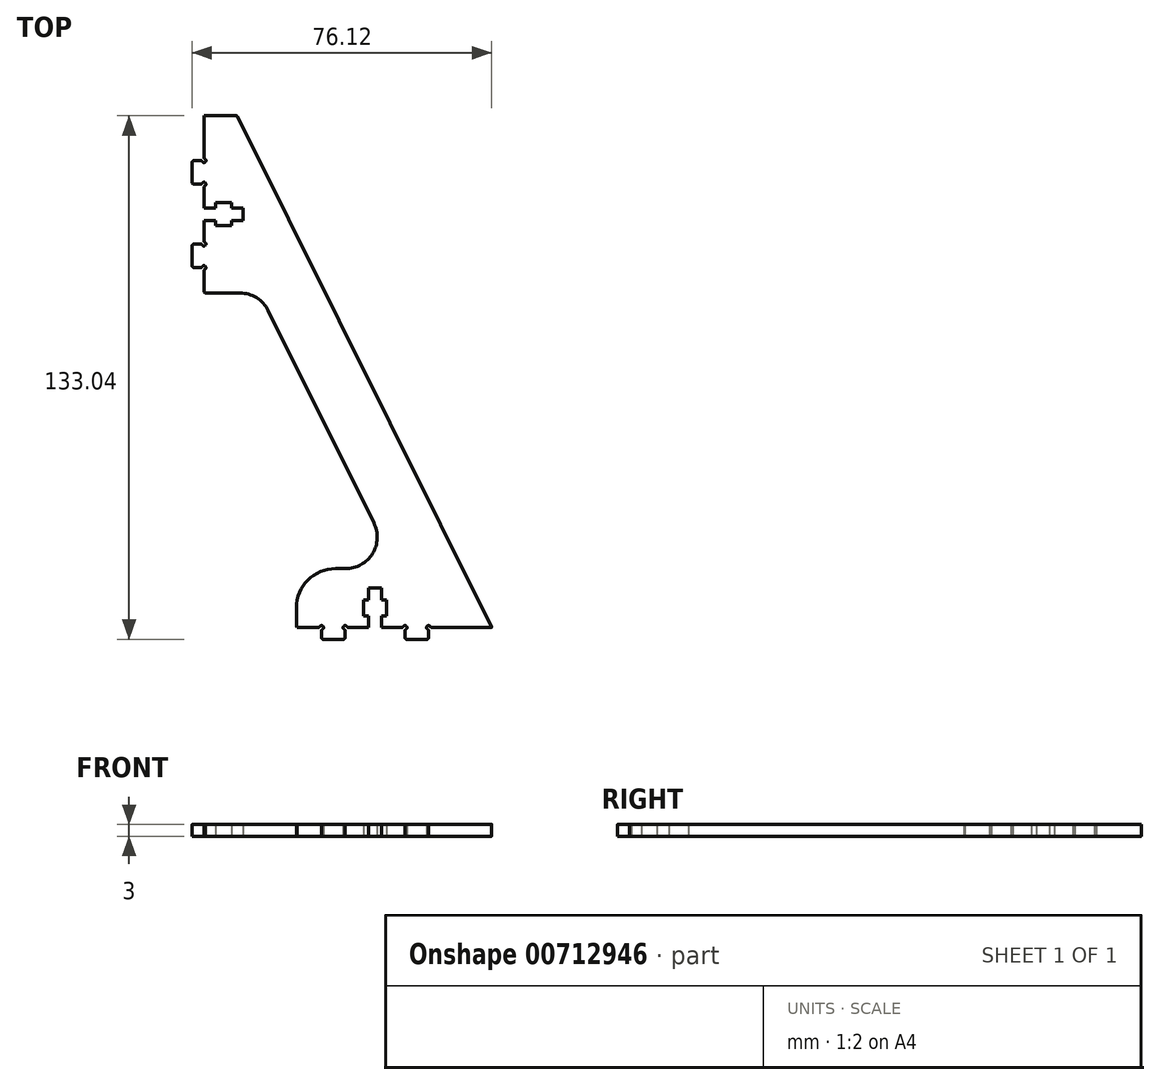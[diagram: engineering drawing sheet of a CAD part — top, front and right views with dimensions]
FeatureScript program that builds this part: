
annotation { "Feature Type Name" : "Feature", "Feature Type Description" : "" }
export const myFeature = defineFeature(function(context is Context, id is Id, definition is map)
    precondition{}
    {
        {
            var Q0;
            Q0=qCreatedBy(makeId("Top.planeOp"),FACE);
            var sketch = newSketch(context, id + "F0", { "sketchPlane" : qUnion([Q0])});
            skArc(sketch, "E0", {"start": v(-6.05, -63.52) * mm, "mid": v(-5.8, -63.45) * mm, "end": v(-5.61, -63.27) * mm});
            skArc(sketch, "E1", {"start": v(-4.93, -63.95) * mm, "mid": v(-4.83, -63.17) * mm, "end": v(-5.61, -63.27) * mm});
            skArc(sketch, "E2", {"start": v(-4.93, -63.95) * mm, "mid": v(-5.11, -64.14) * mm, "end": v(-5.18, -64.39) * mm});
            skLineSegment(sketch, "E3", {"start": v(-5.18, -64.39) * mm, "end": v(-5.18, -66.02) * mm});
            skArc(sketch, "E4", {"start": v(-5.18, -66.02) * mm, "mid": v(-5.04, -66.38) * mm, "end": v(-4.68, -66.52) * mm});
            skLineSegment(sketch, "E5", {"start": v(-4.68, -66.52) * mm, "end": v(0.32, -66.52) * mm});
            skArc(sketch, "E6", {"start": v(0.32, -66.52) * mm, "mid": v(0.67, -66.38) * mm, "end": v(0.82, -66.02) * mm});
            skLineSegment(sketch, "E7", {"start": v(0.82, -66.02) * mm, "end": v(0.82, -64.39) * mm});
            skArc(sketch, "E8", {"start": v(0.82, -64.39) * mm, "mid": v(0.75, -64.14) * mm, "end": v(0.57, -63.95) * mm});
            skArc(sketch, "E9", {"start": v(1.25, -63.27) * mm, "mid": v(0.46, -63.17) * mm, "end": v(0.57, -63.95) * mm});
            skArc(sketch, "E10", {"start": v(1.25, -63.27) * mm, "mid": v(1.43, -63.45) * mm, "end": v(1.68, -63.52) * mm});
            skLineSegment(sketch, "E11", {"start": v(1.68, -63.52) * mm, "end": v(6.82, -63.52) * mm});
            skLineSegment(sketch, "E12", {"start": v(6.82, -63.52) * mm, "end": v(6.82, -60.52) * mm});
            skLineSegment(sketch, "E13", {"start": v(6.82, -60.52) * mm, "end": v(5.54, -60.52) * mm});
            skLineSegment(sketch, "E14", {"start": v(5.54, -60.52) * mm, "end": v(5.54, -56.52) * mm});
            skLineSegment(sketch, "E15", {"start": v(5.54, -56.52) * mm, "end": v(6.82, -56.52) * mm});
            skLineSegment(sketch, "E16", {"start": v(6.82, -56.52) * mm, "end": v(6.82, -53.52) * mm});
            skLineSegment(sketch, "E17", {"start": v(6.82, -53.52) * mm, "end": v(10.02, -53.52) * mm});
            skLineSegment(sketch, "E18", {"start": v(10.02, -53.52) * mm, "end": v(10.02, -56.52) * mm});
            skLineSegment(sketch, "E19", {"start": v(10.02, -56.52) * mm, "end": v(11.3, -56.52) * mm});
            skLineSegment(sketch, "E20", {"start": v(11.3, -56.52) * mm, "end": v(11.3, -60.52) * mm});
            skLineSegment(sketch, "E21", {"start": v(11.3, -60.52) * mm, "end": v(10.02, -60.52) * mm});
            skLineSegment(sketch, "E22", {"start": v(10.02, -60.52) * mm, "end": v(10.02, -63.52) * mm});
            skLineSegment(sketch, "E23", {"start": v(10.02, -63.52) * mm, "end": v(15.15, -63.52) * mm});
            skArc(sketch, "E24", {"start": v(15.15, -63.52) * mm, "mid": v(15.4, -63.45) * mm, "end": v(15.59, -63.27) * mm});
            skArc(sketch, "E25", {"start": v(16.27, -63.95) * mm, "mid": v(16.37, -63.17) * mm, "end": v(15.59, -63.27) * mm});
            skArc(sketch, "E26", {"start": v(16.27, -63.95) * mm, "mid": v(16.09, -64.14) * mm, "end": v(16.02, -64.39) * mm});
            skLineSegment(sketch, "E27", {"start": v(16.02, -64.39) * mm, "end": v(16.02, -66.02) * mm});
            skArc(sketch, "E28", {"start": v(16.02, -66.02) * mm, "mid": v(16.16, -66.38) * mm, "end": v(16.52, -66.52) * mm});
            skLineSegment(sketch, "E29", {"start": v(16.52, -66.52) * mm, "end": v(21.52, -66.52) * mm});
            skArc(sketch, "E30", {"start": v(21.52, -66.52) * mm, "mid": v(21.87, -66.38) * mm, "end": v(22.02, -66.02) * mm});
            skLineSegment(sketch, "E31", {"start": v(22.02, -66.02) * mm, "end": v(22.02, -64.39) * mm});
            skArc(sketch, "E32", {"start": v(22.02, -64.39) * mm, "mid": v(21.95, -64.14) * mm, "end": v(21.77, -63.95) * mm});
            skArc(sketch, "E33", {"start": v(22.45, -63.27) * mm, "mid": v(21.66, -63.17) * mm, "end": v(21.77, -63.95) * mm});
            skArc(sketch, "E34", {"start": v(22.45, -63.27) * mm, "mid": v(22.63, -63.45) * mm, "end": v(22.88, -63.52) * mm});
            skArc(sketch, "E35", {"start": v(-35.06, 55.99) * mm, "mid": v(-35, 55.74) * mm, "end": v(-34.8, 55.56) * mm});
            skArc(sketch, "E36", {"start": v(-35.5, 54.87) * mm, "mid": v(-34.7, 54.77) * mm, "end": v(-34.8, 55.56) * mm});
            skArc(sketch, "E37", {"start": v(-35.5, 54.87) * mm, "mid": v(-35.67, 55.06) * mm, "end": v(-35.92, 55.12) * mm});
            skLineSegment(sketch, "E38", {"start": v(-35.92, 55.12) * mm, "end": v(-37.56, 55.12) * mm});
            skLineSegment(sketch, "E39", {"start": v(-37.56, 49.12) * mm, "end": v(-35.92, 49.12) * mm});
            skArc(sketch, "E40", {"start": v(-35.92, 49.12) * mm, "mid": v(-35.67, 49.19) * mm, "end": v(-35.5, 49.37) * mm});
            skArc(sketch, "E41", {"start": v(-34.8, 48.69) * mm, "mid": v(-34.7, 49.48) * mm, "end": v(-35.5, 49.37) * mm});
            skArc(sketch, "E42", {"start": v(-34.8, 48.69) * mm, "mid": v(-35, 48.5) * mm, "end": v(-35.06, 48.26) * mm});
            skLineSegment(sketch, "E43", {"start": v(-35.06, 48.26) * mm, "end": v(-35.06, 43.12) * mm});
            skLineSegment(sketch, "E44", {"start": v(-35.06, 43.12) * mm, "end": v(-32.06, 43.12) * mm});
            skLineSegment(sketch, "E45", {"start": v(-32.06, 43.12) * mm, "end": v(-32.06, 44.4) * mm});
            skLineSegment(sketch, "E46", {"start": v(-32.06, 44.4) * mm, "end": v(-28.06, 44.4) * mm});
            skLineSegment(sketch, "E47", {"start": v(-28.06, 44.4) * mm, "end": v(-28.06, 43.12) * mm});
            skLineSegment(sketch, "E48", {"start": v(-28.06, 43.12) * mm, "end": v(-25.06, 43.12) * mm});
            skLineSegment(sketch, "E49", {"start": v(-25.06, 43.12) * mm, "end": v(-25.06, 39.92) * mm});
            skLineSegment(sketch, "E50", {"start": v(-25.06, 39.92) * mm, "end": v(-28.06, 39.92) * mm});
            skLineSegment(sketch, "E51", {"start": v(-28.06, 39.92) * mm, "end": v(-28.06, 38.65) * mm});
            skLineSegment(sketch, "E52", {"start": v(-28.06, 38.65) * mm, "end": v(-32.06, 38.65) * mm});
            skLineSegment(sketch, "E53", {"start": v(-32.06, 38.65) * mm, "end": v(-32.06, 39.92) * mm});
            skLineSegment(sketch, "E54", {"start": v(-32.06, 39.92) * mm, "end": v(-35.06, 39.92) * mm});
            skLineSegment(sketch, "E55", {"start": v(-35.06, 39.92) * mm, "end": v(-35.06, 34.79) * mm});
            skArc(sketch, "E56", {"start": v(-35.06, 34.79) * mm, "mid": v(-35, 34.54) * mm, "end": v(-34.8, 34.36) * mm});
            skArc(sketch, "E57", {"start": v(-35.5, 33.67) * mm, "mid": v(-34.7, 33.57) * mm, "end": v(-34.8, 34.36) * mm});
            skArc(sketch, "E58", {"start": v(-35.5, 33.67) * mm, "mid": v(-35.67, 33.86) * mm, "end": v(-35.92, 33.92) * mm});
            skLineSegment(sketch, "E59", {"start": v(-35.92, 33.92) * mm, "end": v(-37.56, 33.92) * mm});
            skLineSegment(sketch, "E60", {"start": v(-37.56, 27.92) * mm, "end": v(-35.92, 27.92) * mm});
            skArc(sketch, "E61", {"start": v(-35.92, 27.92) * mm, "mid": v(-35.67, 27.99) * mm, "end": v(-35.5, 28.17) * mm});
            skArc(sketch, "E62", {"start": v(-34.8, 27.49) * mm, "mid": v(-34.7, 28.28) * mm, "end": v(-35.5, 28.17) * mm});
            skArc(sketch, "E63", {"start": v(-34.8, 27.49) * mm, "mid": v(-35, 27.3) * mm, "end": v(-35.06, 27.06) * mm});
            skArc(sketch, "E64", {"start": v(-37.56, 55.12) * mm, "mid": v(-37.91, 54.98) * mm, "end": v(-38.06, 54.62) * mm});
            skLineSegment(sketch, "E65", {"start": v(-38.06, 54.62) * mm, "end": v(-38.06, 49.62) * mm});
            skArc(sketch, "E66", {"start": v(-38.06, 49.62) * mm, "mid": v(-37.91, 49.27) * mm, "end": v(-37.56, 49.12) * mm});
            skArc(sketch, "E67", {"start": v(-37.56, 33.92) * mm, "mid": v(-37.91, 33.78) * mm, "end": v(-38.06, 33.42) * mm});
            skLineSegment(sketch, "E68", {"start": v(-38.06, 33.42) * mm, "end": v(-38.06, 28.42) * mm});
            skArc(sketch, "E69", {"start": v(-38.06, 28.42) * mm, "mid": v(-37.91, 28.07) * mm, "end": v(-37.56, 27.92) * mm});
            skLineSegment(sketch, "E70", {"start": v(-35.06, 66.52) * mm, "end": v(-35.06, 55.99) * mm});
            skArc(sketch, "E71", {"start": v(-1.58, -48.52) * mm, "mid": v(-8.65, -51.45) * mm, "end": v(-11.58, -58.52) * mm});
            skLineSegment(sketch, "E72", {"start": v(-35.06, 66.52) * mm, "end": v(-26.91, 66.52) * mm});
            skArc(sketch, "E73", {"start": v(-26.47, 66.25) * mm, "mid": v(-26.65, 66.45) * mm, "end": v(-26.91, 66.52) * mm});
            skLineSegment(sketch, "E74", {"start": v(22.88, -63.52) * mm, "end": v(37.96, -63.52) * mm});
            skLineSegment(sketch, "E75", {"start": v(-26.47, 66.25) * mm, "end": v(38.05, -63.38) * mm});
            skArc(sketch, "E76", {"start": v(37.96, -63.52) * mm, "mid": v(38.04, -63.47) * mm, "end": v(38.05, -63.38) * mm});
            skLineSegment(sketch, "E77", {"start": v(-1.58, -48.52) * mm, "end": v(0.98, -48.52) * mm});
            skArc(sketch, "E78", {"start": v(0.98, -48.52) * mm, "mid": v(7.78, -44.73) * mm, "end": v(8.14, -36.96) * mm});
            skLineSegment(sketch, "E79", {"start": v(-18.73, 17.04) * mm, "end": v(8.14, -36.96) * mm});
            skArc(sketch, "E80", {"start": v(-18.73, 17.04) * mm, "mid": v(-21.68, 20.28) * mm, "end": v(-25.9, 21.48) * mm});
            skLineSegment(sketch, "E81", {"start": v(-11.58, -63.27) * mm, "end": v(-11.58, -58.52) * mm});
            skLineSegment(sketch, "E82", {"start": v(-11.33, -63.52) * mm, "end": v(-6.05, -63.52) * mm});
            skLineSegment(sketch, "E83", {"start": v(-11.58, -63.27) * mm, "end": v(-11.33, -63.52) * mm});
            skLineSegment(sketch, "E84", {"start": v(-35.06, 27.06) * mm, "end": v(-35.06, 21.73) * mm});
            skLineSegment(sketch, "E85", {"start": v(-34.8, 21.48) * mm, "end": v(-25.9, 21.48) * mm});
            skLineSegment(sketch, "E86", {"start": v(-35.06, 21.73) * mm, "end": v(-34.8, 21.48) * mm});
            skSolve(sketch);
        }
        {
            var Q0;
            Q0 = qSketchRegion(id + "F0", true);
            extrude(context, id + "F1", {"entities" : qUnion([Q0]), "depth" : 3 * mm, "offsetDistance" : 25 * mm});
        }
    });
